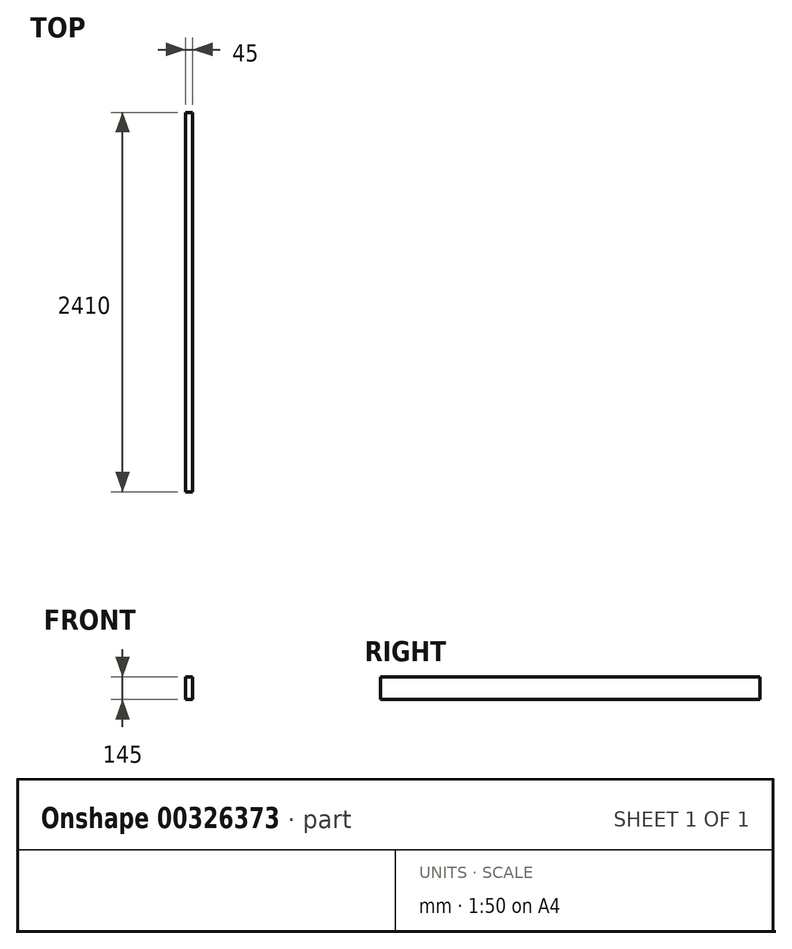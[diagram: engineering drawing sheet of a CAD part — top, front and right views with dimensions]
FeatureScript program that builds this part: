
annotation { "Feature Type Name" : "Feature", "Feature Type Description" : "" }
export const myFeature = defineFeature(function(context is Context, id is Id, definition is map)
    precondition{}
    {
        {
            var Q0;
            Q0=qCreatedBy(makeId("Front.planeOp"),FACE);
            var sketch = newSketch(context, id + "F0", { "sketchPlane" : qUnion([Q0])});
            skLineSegment(sketch, "E0.bottom", {"start": v(0, 0) * mm, "end": v(45, 0) * mm});
            skLineSegment(sketch, "E0.top", {"start": v(0, 145) * mm, "end": v(45, 145) * mm});
            skLineSegment(sketch, "E0.left", {"start": v(0, 0) * mm, "end": v(0, 145) * mm});
            skLineSegment(sketch, "E0.right", {"start": v(45, 0) * mm, "end": v(45, 145) * mm});
            skSolve(sketch);
        }
        {
            var Q0;
            Q0=makeQuery(id+"F0.imprint","IMPRINT",FACE,{"disambiguationData":[TD([[makeQuery(id+"F0.imprint","IMPRINT",EDGE,{"derivedFrom":sQuery(id+"F0.wireOp",EDGE,"E0.bottom")}),1.0]])]});
            extrude(context, id + "F1", {"entities" : qUnion([Q0]), "depth" : 2410 * mm});
        }
    });
